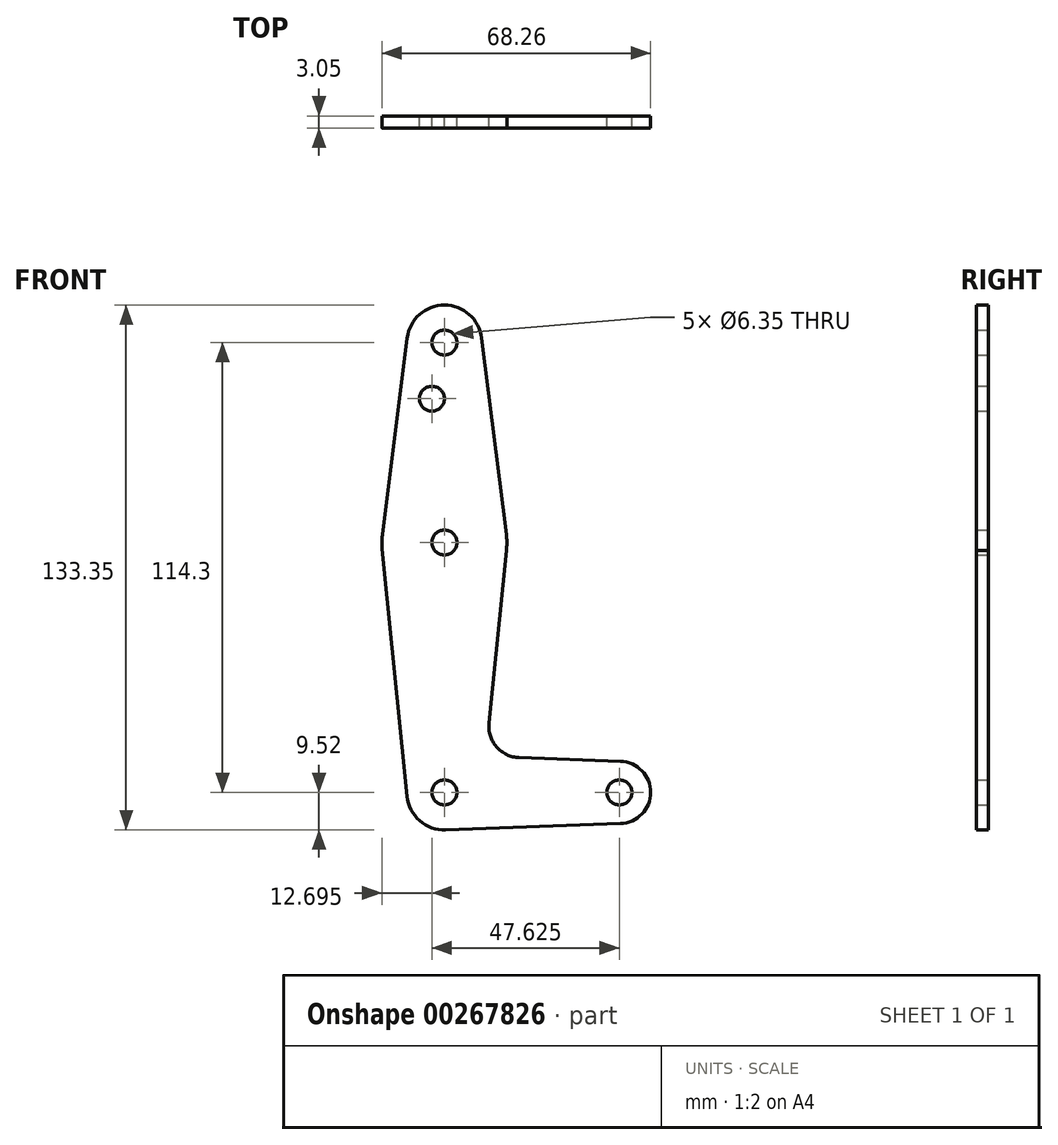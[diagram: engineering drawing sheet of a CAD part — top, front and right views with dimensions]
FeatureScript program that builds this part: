
annotation { "Feature Type Name" : "Feature", "Feature Type Description" : "" }
export const myFeature = defineFeature(function(context is Context, id is Id, definition is map)
    precondition{}
    {
        {
            var Q0;
            Q0=qCreatedBy(makeId("Front.planeOp"),FACE);
            var sketch = newSketch(context, id + "F0", { "sketchPlane" : qUnion([Q0])});
            skLineSegment(sketch, "E0", {"start": v(0, 0) * mm, "end": v(44.45, 0) * mm, "construction": true});
            skLineSegment(sketch, "E1", {"start": v(0, 0) * mm, "end": v(0, 114.3) * mm, "construction": true});
            skCircle(sketch, "E2", {"center": v(0, 114.3) * mm, "radius": 9.53 * mm});
            skCircle(sketch, "E3", {"center": v(0, 63.5) * mm, "radius": 15.88 * mm});
            skCircle(sketch, "E4", {"center": v(44.45, 0) * mm, "radius": 7.94 * mm});
            skCircle(sketch, "E5", {"center": v(0, 0) * mm, "radius": 9.53 * mm});
            skLineSegment(sketch, "E6", {"start": v(15.75, 65.48) * mm, "end": v(9.45, 115.5) * mm});
            skLineSegment(sketch, "E7", {"start": v(-15.8, 61.91) * mm, "end": v(-9.48, -0.95) * mm});
            skLineSegment(sketch, "E8", {"start": v(-15.75, 65.48) * mm, "end": v(-9.45, 115.5) * mm});
            skLineSegment(sketch, "E9", {"start": v(15.75, 61.52) * mm, "end": v(11.34, 17.6) * mm});
            skLineSegment(sketch, "E10", {"start": v(18.97, 8.85) * mm, "end": v(44.73, 7.93) * mm});
            skLineSegment(sketch, "E11", {"start": v(44.73, -7.93) * mm, "end": v(0.34, -9.52) * mm});
            skArc(sketch, "E12.filletArc", {"start": v(11.34, 17.6) * mm, "mid": v(13.26, 11.57) * mm, "end": v(18.97, 8.85) * mm});
            skCircle(sketch, "E13", {"center": v(0, 114.3) * mm, "radius": 3.18 * mm});
            skCircle(sketch, "E14", {"center": v(0, 63.5) * mm, "radius": 3.18 * mm});
            skCircle(sketch, "E15", {"center": v(0, 0) * mm, "radius": 3.18 * mm});
            skCircle(sketch, "E16", {"center": v(44.45, 0) * mm, "radius": 3.18 * mm});
            skCircle(sketch, "E17", {"center": v(-3.18, 100.03) * mm, "radius": 3.18 * mm});
            skSolve(sketch);
        }
        {
            var Q0;
            Q0 = qSketchRegion(id + "F0", true);
            extrude(context, id + "F1", {"entities" : qUnion([Q0]), "depth" : 3.05 * mm});
        }
    });
